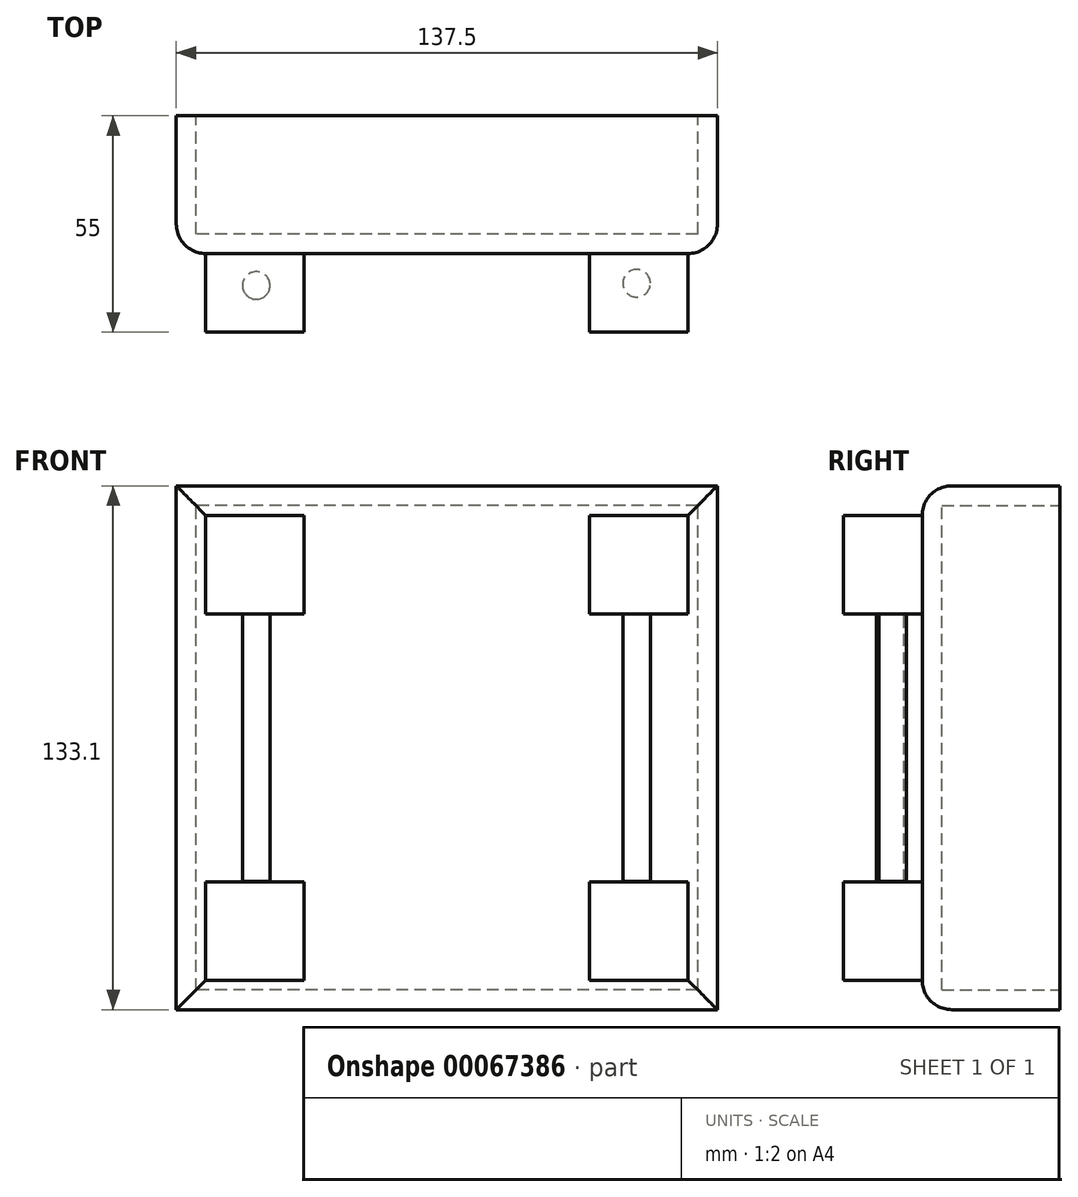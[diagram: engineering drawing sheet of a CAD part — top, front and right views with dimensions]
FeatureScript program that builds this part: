
annotation { "Feature Type Name" : "Feature", "Feature Type Description" : "" }
export const myFeature = defineFeature(function(context is Context, id is Id, definition is map)
    precondition{}
    {
        {
            var Q0;
            Q0=qCreatedBy(makeId("Front.planeOp"),FACE);
            var sketch = newSketch(context, id + "F0", { "sketchPlane" : qUnion([Q0])});
            skLineSegment(sketch, "E0.rect.bottom", {"start": v(68.75, -66.55) * mm, "end": v(-68.75, -66.55) * mm});
            skLineSegment(sketch, "E0.rect.top", {"start": v(68.75, 66.55) * mm, "end": v(-68.75, 66.55) * mm});
            skLineSegment(sketch, "E0.rect.left", {"start": v(68.75, -66.55) * mm, "end": v(68.75, 66.55) * mm});
            skLineSegment(sketch, "E0.rect.right", {"start": v(-68.75, -66.55) * mm, "end": v(-68.75, 66.55) * mm});
            skPoint(sketch, "E0.rect.middle", {"position": v(0, 0) * mm});
            skSolve(sketch);
        }
        {
            var Q0;
            Q0=makeQuery(id+"F0.imprint","IMPRINT",FACE,{"disambiguationData":[TD([[makeQuery(id+"F0.imprint","IMPRINT",EDGE,{"derivedFrom":sQuery(id+"F0.wireOp",EDGE,"E0.rect.bottom")}),-1.0]])]});
            var Q1;
            Q1=sQuery(id+"F0.wireOp",EDGE,"E0.rect.top");
            extrude(context, id + "F1", {"entities" : qUnion([Q0]), "surfaceEntities" : qUnion([Q1]), "endBound" : BoundingType.SYMMETRIC, "depth" : 35 * mm});
        }
        {
            var Q0;
            Q0=makeQuery(id+"F1.opExtrude","CAP_FACE",FACE,{"disambiguationData":[OSD([sQuery(id+"F0.wireOp",EDGE,"E0.rect.bottom"),sQuery(id+"F0.wireOp",EDGE,"E0.rect.top"),sQuery(id+"F0.wireOp",EDGE,"E0.rect.left"),sQuery(id+"F0.wireOp",EDGE,"E0.rect.right")])],"isStart":true});
            shell(context, id + "F2", {"entities" : qUnion([Q0]), "thickness" : 5 * mm});
        }
        {
            var Q0;
            Q0=makeQuery(id+"F1.opExtrude","CAP_FACE",FACE,{"disambiguationData":[OSD([sQuery(id+"F0.wireOp",EDGE,"E0.rect.bottom"),sQuery(id+"F0.wireOp",EDGE,"E0.rect.top"),sQuery(id+"F0.wireOp",EDGE,"E0.rect.left"),sQuery(id+"F0.wireOp",EDGE,"E0.rect.right")])],"isStart":false});
            fillet(context, id + "F3", {"entities" : qUnion([Q0]), "radius" : 7.5 * mm, "tangentPropagation" : true, "allowEdgeOverflow" : false});
        }
        {
            var Q0;
            Q0=makeQuery(id+"F1.opExtrude","CAP_FACE",FACE,{"disambiguationData":[OSD([sQuery(id+"F0.wireOp",EDGE,"E0.rect.bottom"),sQuery(id+"F0.wireOp",EDGE,"E0.rect.top"),sQuery(id+"F0.wireOp",EDGE,"E0.rect.left"),sQuery(id+"F0.wireOp",EDGE,"E0.rect.right")])],"isStart":false});
            var sketch = newSketch(context, id + "F4", { "sketchPlane" : qUnion([Q0])});
            skLineSegment(sketch, "E1.bottom", {"start": v(-61.25, 59.05) * mm, "end": v(-36.25, 59.05) * mm});
            skLineSegment(sketch, "E1.top", {"start": v(-61.25, 34.05) * mm, "end": v(-36.25, 34.05) * mm});
            skLineSegment(sketch, "E1.left", {"start": v(-61.25, 59.05) * mm, "end": v(-61.25, 34.05) * mm});
            skLineSegment(sketch, "E1.right", {"start": v(-36.25, 59.05) * mm, "end": v(-36.25, 34.05) * mm});
            skSolve(sketch);
        }
        {
            var Q0;
            Q0 = qSketchRegion(id + "F4", true);
            extrude(context, id + "F5", {"entities" : qUnion([Q0]), "operationType" : NewBodyOperationType.ADD, "depth" : 20 * mm});
        }
        {
            var Q0;
            Q0=makeQuery(id+"F1.opExtrude","CAP_FACE",FACE,{"disambiguationData":[OSD([sQuery(id+"F0.wireOp",EDGE,"E0.rect.bottom"),sQuery(id+"F0.wireOp",EDGE,"E0.rect.top"),sQuery(id+"F0.wireOp",EDGE,"E0.rect.left"),sQuery(id+"F0.wireOp",EDGE,"E0.rect.right")])],"isStart":false});
            var sketch = newSketch(context, id + "F6", { "sketchPlane" : qUnion([Q0])});
            skLineSegment(sketch, "E2.bottom", {"start": v(61.25, 59.05) * mm, "end": v(36.25, 59.05) * mm});
            skLineSegment(sketch, "E2.top", {"start": v(61.25, 34.05) * mm, "end": v(36.25, 34.05) * mm});
            skLineSegment(sketch, "E2.left", {"start": v(61.25, 59.05) * mm, "end": v(61.25, 34.05) * mm});
            skLineSegment(sketch, "E2.right", {"start": v(36.25, 59.05) * mm, "end": v(36.25, 34.05) * mm});
            skSolve(sketch);
        }
        {
            var Q0;
            Q0 = qSketchRegion(id + "F6", true);
            extrude(context, id + "F7", {"entities" : qUnion([Q0]), "operationType" : NewBodyOperationType.ADD, "depth" : 20 * mm});
        }
        {
            var Q0;
            Q0=makeQuery(id+"F1.opExtrude","CAP_FACE",FACE,{"disambiguationData":[OSD([sQuery(id+"F0.wireOp",EDGE,"E0.rect.bottom"),sQuery(id+"F0.wireOp",EDGE,"E0.rect.top"),sQuery(id+"F0.wireOp",EDGE,"E0.rect.left"),sQuery(id+"F0.wireOp",EDGE,"E0.rect.right")])],"isStart":false});
            var sketch = newSketch(context, id + "F8", { "sketchPlane" : qUnion([Q0])});
            skLineSegment(sketch, "E3.bottom", {"start": v(-61.25, -59.05) * mm, "end": v(-36.25, -59.05) * mm});
            skLineSegment(sketch, "E3.top", {"start": v(-61.25, -34.05) * mm, "end": v(-36.25, -34.05) * mm});
            skLineSegment(sketch, "E3.left", {"start": v(-61.25, -59.05) * mm, "end": v(-61.25, -34.05) * mm});
            skLineSegment(sketch, "E3.right", {"start": v(-36.25, -59.05) * mm, "end": v(-36.25, -34.05) * mm});
            skSolve(sketch);
        }
        {
            var Q0;
            Q0 = qSketchRegion(id + "F8", true);
            extrude(context, id + "F9", {"entities" : qUnion([Q0]), "operationType" : NewBodyOperationType.ADD, "depth" : 20 * mm});
        }
        {
            var Q0;
            Q0=makeQuery(id+"F1.opExtrude","CAP_FACE",FACE,{"disambiguationData":[OSD([sQuery(id+"F0.wireOp",EDGE,"E0.rect.bottom"),sQuery(id+"F0.wireOp",EDGE,"E0.rect.top"),sQuery(id+"F0.wireOp",EDGE,"E0.rect.left"),sQuery(id+"F0.wireOp",EDGE,"E0.rect.right")])],"isStart":false});
            var sketch = newSketch(context, id + "F10", { "sketchPlane" : qUnion([Q0])});
            skLineSegment(sketch, "E4.bottom", {"start": v(61.25, -59.05) * mm, "end": v(36.25, -59.05) * mm});
            skLineSegment(sketch, "E4.top", {"start": v(61.25, -34.05) * mm, "end": v(36.25, -34.05) * mm});
            skLineSegment(sketch, "E4.left", {"start": v(61.25, -59.05) * mm, "end": v(61.25, -34.05) * mm});
            skLineSegment(sketch, "E4.right", {"start": v(36.25, -59.05) * mm, "end": v(36.25, -34.05) * mm});
            skSolve(sketch);
        }
        {
            var Q0;
            Q0 = qSketchRegion(id + "F10", true);
            extrude(context, id + "F11", {"entities" : qUnion([Q0]), "operationType" : NewBodyOperationType.ADD, "depth" : 20 * mm});
        }
        {
            var Q0;
            {var subQ1=sQuery(id+"F0.wireOp",EDGE,"E0.rect.right");var subQ3=sQuery(id+"F4.wireOp",EDGE,"E1.top");Q0=makeQuery(id+"F5.boolean.opBoolean","SPLIT",FACE,{"disambiguationData":[TD([makeQuery(id+"F3.opFillet","BLEND_FACE",FACE,{"disambiguationData":[OSD([subQ1])]})])],"derivedFrom":makeQuery(id+"F5.opExtrude","SWEPT_FACE",FACE,{"disambiguationData":[OSD([subQ3])]})});}
            var sketch = newSketch(context, id + "F12", { "sketchPlane" : qUnion([Q0])});
            skCircle(sketch, "E5", {"center": v(-48.42, 25.62) * mm, "radius": 3.5 * mm});
            skSolve(sketch);
        }
        {
            var Q0;
            Q0 = qSketchRegion(id + "F12", true);
            extrude(context, id + "F13", {"entities" : qUnion([Q0]), "operationType" : NewBodyOperationType.ADD, "depth" : 68 * mm});
        }
        {
            var Q0;
            {var subQ2=sQuery(id+"F6.wireOp",EDGE,"E2.top");var subQ3=sQuery(id+"F0.wireOp",EDGE,"E0.rect.left");Q0=makeQuery(id+"F7.boolean.opBoolean","SPLIT",FACE,{"disambiguationData":[TD([makeQuery(id+"F3.opFillet","BLEND_FACE",FACE,{"disambiguationData":[OSD([subQ3])]})])],"derivedFrom":makeQuery(id+"F7.opExtrude","SWEPT_FACE",FACE,{"disambiguationData":[OSD([subQ2])]})});}
            var sketch = newSketch(context, id + "F14", { "sketchPlane" : qUnion([Q0])});
            skCircle(sketch, "E6", {"center": v(48.2, 25.03) * mm, "radius": 3.5 * mm});
            skSolve(sketch);
        }
        {
            var Q0;
            Q0 = qSketchRegion(id + "F14", true);
            extrude(context, id + "F15", {"entities" : qUnion([Q0]), "operationType" : NewBodyOperationType.ADD, "depth" : 68 * mm});
        }
    });
